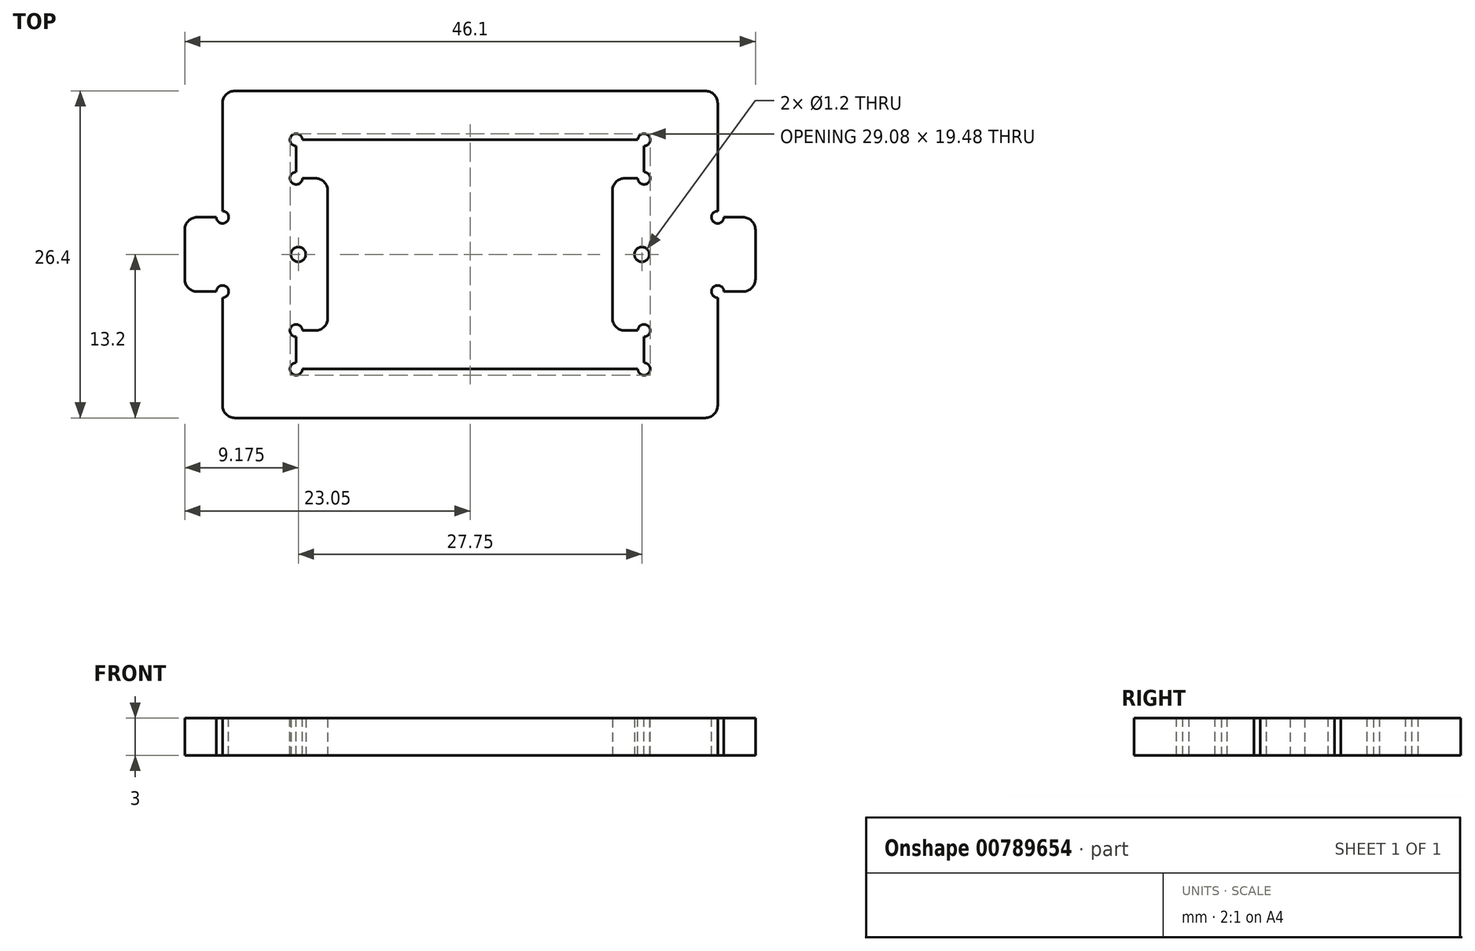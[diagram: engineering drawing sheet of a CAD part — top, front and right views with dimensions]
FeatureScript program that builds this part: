
annotation { "Feature Type Name" : "Feature", "Feature Type Description" : "" }
export const myFeature = defineFeature(function(context is Context, id is Id, definition is map)
    precondition{}
    {
        {
            var Q0;
            Q0=qCreatedBy(makeId("Top.planeOp"),FACE);
            var sketch = newSketch(context, id + "F0", { "sketchPlane" : qUnion([Q0])});
            skLineSegment(sketch, "E0", {"start": v(0, 0) * mm, "end": v(0, 13.2) * mm, "construction": true});
            skLineSegment(sketch, "E1.MirrorCS", {"start": v(-20, -13.2) * mm, "end": v(0, -13.2) * mm});
            skLineSegment(sketch, "E2.MirrorCS", {"start": v(20, -13.2) * mm, "end": v(0, -13.2) * mm});
            skCircle(sketch, "E3", {"center": v(-13.88, 0) * mm, "radius": 0.6 * mm});
            skCircle(sketch, "E4.MirrorC", {"center": v(13.88, 0) * mm, "radius": 0.6 * mm});
            skLineSegment(sketch, "E5", {"start": v(-20, 13.2) * mm, "end": v(20, 13.2) * mm});
            skLineSegment(sketch, "E6", {"start": v(-20, 13.2) * mm, "end": v(-20, -13.2) * mm});
            skLineSegment(sketch, "E7", {"start": v(20, 13.2) * mm, "end": v(20, -13.2) * mm});
            skLineSegment(sketch, "E8", {"start": v(0, 0) * mm, "end": v(-20, 0) * mm, "construction": true});
            skLineSegment(sketch, "E9.bottom", {"start": v(-14.05, 9.25) * mm, "end": v(14.05, 9.25) * mm});
            skLineSegment(sketch, "E9.top", {"start": v(-14.05, 6.15) * mm, "end": v(-11.5, 6.15) * mm});
            skLineSegment(sketch, "E9.left", {"start": v(-14.05, 9.25) * mm, "end": v(-14.05, 6.15) * mm});
            skLineSegment(sketch, "E9.right", {"start": v(14.05, 9.25) * mm, "end": v(14.05, 6.15) * mm});
            skLineSegment(sketch, "E10.MirrorCS", {"start": v(-14.05, -9.25) * mm, "end": v(14.05, -9.25) * mm});
            skLineSegment(sketch, "E11.MirrorCS", {"start": v(-14.05, -6.15) * mm, "end": v(-11.5, -6.15) * mm});
            skLineSegment(sketch, "E12.MirrorCS", {"start": v(-14.05, -9.25) * mm, "end": v(-14.05, -6.15) * mm});
            skLineSegment(sketch, "E13.MirrorCS", {"start": v(14.05, -9.25) * mm, "end": v(14.05, -6.15) * mm});
            skLineSegment(sketch, "E14", {"start": v(-11.5, 6.15) * mm, "end": v(-11.5, -6.15) * mm});
            skLineSegment(sketch, "E15", {"start": v(11.5, 6.15) * mm, "end": v(11.5, -6.15) * mm});
            skLineSegment(sketch, "E16.trimOffspring", {"start": v(11.5, 6.15) * mm, "end": v(14.05, 6.15) * mm});
            skLineSegment(sketch, "E17.trimOffspring", {"start": v(11.5, -6.15) * mm, "end": v(14.05, -6.15) * mm});
            skSolve(sketch);
        }
        {
            var Q0;
            Q0=makeQuery(id+"F0.imprint","IMPRINT",FACE,{"disambiguationData":[TD([[makeQuery(id+"F0.imprint","IMPRINT",EDGE,{"derivedFrom":sQuery(id+"F0.wireOp",EDGE,"E1.MirrorCS")}),1.0]])]});
            extrude(context, id + "F1", {"entities" : qUnion([Q0]), "depth" : 3 * mm, "offsetDistance" : 25 * mm});
        }
        {
            var Q0;
            Q0=makeQuery(id+"F1.opExtrude","CAP_FACE",FACE,{"disambiguationData":[OSD([sQuery(id+"F0.wireOp",EDGE,"E1.MirrorCS"),sQuery(id+"F0.wireOp",EDGE,"E2.MirrorCS"),sQuery(id+"F0.wireOp",EDGE,"E3"),sQuery(id+"F0.wireOp",EDGE,"E4.MirrorC"),sQuery(id+"F0.wireOp",EDGE,"E5"),sQuery(id+"F0.wireOp",EDGE,"E6"),sQuery(id+"F0.wireOp",EDGE,"E7"),sQuery(id+"F0.wireOp",EDGE,"E9.bottom"),sQuery(id+"F0.wireOp",EDGE,"E9.top"),sQuery(id+"F0.wireOp",EDGE,"E9.left"),sQuery(id+"F0.wireOp",EDGE,"E9.right"),sQuery(id+"F0.wireOp",EDGE,"E10.MirrorCS"),sQuery(id+"F0.wireOp",EDGE,"E11.MirrorCS"),sQuery(id+"F0.wireOp",EDGE,"E12.MirrorCS"),sQuery(id+"F0.wireOp",EDGE,"E13.MirrorCS"),sQuery(id+"F0.wireOp",EDGE,"E14"),sQuery(id+"F0.wireOp",EDGE,"E15"),sQuery(id+"F0.wireOp",EDGE,"E16.trimOffspring"),sQuery(id+"F0.wireOp",EDGE,"E17.trimOffspring")])],"isStart":true});
            var sketch = newSketch(context, id + "F2", { "sketchPlane" : qUnion([Q0])});
            skLineSegment(sketch, "E18.bottom", {"start": v(-20, -3) * mm, "end": v(-23.05, -3) * mm});
            skLineSegment(sketch, "E18.top", {"start": v(-20, 3) * mm, "end": v(-23.05, 3) * mm});
            skLineSegment(sketch, "E18.left", {"start": v(-20, -3) * mm, "end": v(-20, 3) * mm});
            skLineSegment(sketch, "E18.right", {"start": v(-23.05, -3) * mm, "end": v(-23.05, 3) * mm});
            skLineSegment(sketch, "E19.MirrorCS", {"start": v(20, 3) * mm, "end": v(23.05, 3) * mm});
            skLineSegment(sketch, "E20.MirrorCS", {"start": v(20, -3) * mm, "end": v(20, 3) * mm});
            skLineSegment(sketch, "E21.MirrorCS", {"start": v(23.05, -3) * mm, "end": v(23.05, 3) * mm});
            skLineSegment(sketch, "E22.MirrorCS", {"start": v(20, -3) * mm, "end": v(23.05, -3) * mm});
            skSolve(sketch);
        }
        {
            var Q0;
            Q0 = qSketchRegion(id + "F2", true);
            var Q1;
            Q1=makeQuery(id+"F1.opExtrude","CAP_FACE",FACE,{"disambiguationData":[OSD([sQuery(id+"F0.wireOp",EDGE,"E1.MirrorCS"),sQuery(id+"F0.wireOp",EDGE,"E2.MirrorCS"),sQuery(id+"F0.wireOp",EDGE,"E3"),sQuery(id+"F0.wireOp",EDGE,"E4.MirrorC"),sQuery(id+"F0.wireOp",EDGE,"E5"),sQuery(id+"F0.wireOp",EDGE,"E6"),sQuery(id+"F0.wireOp",EDGE,"E7"),sQuery(id+"F0.wireOp",EDGE,"E9.bottom"),sQuery(id+"F0.wireOp",EDGE,"E9.top"),sQuery(id+"F0.wireOp",EDGE,"E9.left"),sQuery(id+"F0.wireOp",EDGE,"E9.right"),sQuery(id+"F0.wireOp",EDGE,"E10.MirrorCS"),sQuery(id+"F0.wireOp",EDGE,"E11.MirrorCS"),sQuery(id+"F0.wireOp",EDGE,"E12.MirrorCS"),sQuery(id+"F0.wireOp",EDGE,"E13.MirrorCS"),sQuery(id+"F0.wireOp",EDGE,"E14"),sQuery(id+"F0.wireOp",EDGE,"E15"),sQuery(id+"F0.wireOp",EDGE,"E16.trimOffspring"),sQuery(id+"F0.wireOp",EDGE,"E17.trimOffspring")])],"isStart":false});
            extrude(context, id + "F3", {"entities" : qUnion([Q0]), "operationType" : NewBodyOperationType.ADD, "endBound" : BoundingType.UP_TO_SURFACE, "oppositeDirection" : true, "depth" : 25 * mm, "endBoundEntityFace" : qUnion([Q1]), "offsetDistance" : 25 * mm});
        }
        {
            var Q0;
            {var subQ0=sQuery(id+"F0.wireOp",EDGE,"E17.trimOffspring");var subQ1=sQuery(id+"F0.wireOp",EDGE,"E16.trimOffspring");var subQ2=sQuery(id+"F0.wireOp",EDGE,"E15");var subQ3=sQuery(id+"F0.wireOp",EDGE,"E14");var subQ4=sQuery(id+"F0.wireOp",EDGE,"E13.MirrorCS");var subQ5=sQuery(id+"F0.wireOp",EDGE,"E12.MirrorCS");var subQ6=sQuery(id+"F0.wireOp",EDGE,"E11.MirrorCS");var subQ7=sQuery(id+"F0.wireOp",EDGE,"E10.MirrorCS");var subQ8=sQuery(id+"F0.wireOp",EDGE,"E9.right");var subQ9=sQuery(id+"F0.wireOp",EDGE,"E9.left");var subQ10=sQuery(id+"F0.wireOp",EDGE,"E9.top");var subQ11=sQuery(id+"F0.wireOp",EDGE,"E9.bottom");var subQ12=sQuery(id+"F0.wireOp",EDGE,"E7");var subQ13=sQuery(id+"F0.wireOp",EDGE,"E6");var subQ14=sQuery(id+"F0.wireOp",EDGE,"E5");var subQ15=sQuery(id+"F0.wireOp",EDGE,"E4.MirrorC");var subQ16=sQuery(id+"F0.wireOp",EDGE,"E3");var subQ17=sQuery(id+"F0.wireOp",EDGE,"E2.MirrorCS");var subQ18=sQuery(id+"F0.wireOp",EDGE,"E1.MirrorCS");Q0=makeQuery(id+"F3.boolean.opBoolean","MERGE",FACE,{"derivedFrom":[makeQuery(id+"F1.opExtrude","CAP_FACE",FACE,{"disambiguationData":[OSD([subQ18,subQ17,subQ16,subQ15,subQ14,subQ13,subQ12,subQ11,subQ10,subQ9,subQ8,subQ7,subQ6,subQ5,subQ4,subQ3,subQ2,subQ1,subQ0])],"isStart":false}),makeQuery(id+"F3.opExtrude","CAP_FACE",FACE,{"disambiguationData":[OSD([subQ18,subQ17,subQ16,subQ15,subQ14,subQ13,subQ12,subQ11,subQ10,subQ9,subQ8,subQ7,subQ6,subQ5,subQ4,subQ3,subQ2,subQ1,subQ0]),OD(0.0)],"isStart":false}),makeQuery(id+"F3.opExtrude","CAP_FACE",FACE,{"disambiguationData":[OSD([subQ18,subQ17,subQ16,subQ15,subQ14,subQ13,subQ12,subQ11,subQ10,subQ9,subQ8,subQ7,subQ6,subQ5,subQ4,subQ3,subQ2,subQ1,subQ0]),OD(1.0)],"isStart":false})]});}
            var sketch = newSketch(context, id + "F4", { "sketchPlane" : qUnion([Q0])});
            skPoint(sketch, "E23", {"position": v(-20, 3) * mm});
            skPoint(sketch, "E24", {"position": v(-20, -3) * mm});
            skPoint(sketch, "E25", {"position": v(-14.05, -6.15) * mm});
            skPoint(sketch, "E26", {"position": v(-14.05, -9.25) * mm});
            skPoint(sketch, "E27", {"position": v(-14.05, 9.25) * mm});
            skPoint(sketch, "E28", {"position": v(-14.05, 6.15) * mm});
            skPoint(sketch, "E29", {"position": v(14.05, 9.25) * mm});
            skPoint(sketch, "E30", {"position": v(14.05, 6.15) * mm});
            skPoint(sketch, "E31", {"position": v(14.05, -6.15) * mm});
            skPoint(sketch, "E32", {"position": v(14.05, -9.25) * mm});
            skPoint(sketch, "E33", {"position": v(20, -3) * mm});
            skPoint(sketch, "E34", {"position": v(20, 3) * mm});
            skSolve(sketch);
        }
        {
            var Q0;
            Q0=sQuery(id+"F4.wireOp",VERTEX,"E27");
            var Q1;
            Q1=sQuery(id+"F4.wireOp",VERTEX,"E28");
            var Q2;
            Q2=sQuery(id+"F4.wireOp",VERTEX,"E23");
            var Q3;
            Q3=sQuery(id+"F4.wireOp",VERTEX,"E24");
            var Q4;
            Q4=sQuery(id+"F4.wireOp",VERTEX,"E25");
            var Q5;
            Q5=sQuery(id+"F4.wireOp",VERTEX,"E26");
            var Q6;
            Q6=sQuery(id+"F4.wireOp",VERTEX,"E31");
            var Q7;
            Q7=sQuery(id+"F4.wireOp",VERTEX,"E32");
            var Q8;
            Q8=sQuery(id+"F4.wireOp",VERTEX,"E33");
            var Q9;
            Q9=sQuery(id+"F4.wireOp",VERTEX,"E34");
            var Q10;
            Q10=sQuery(id+"F4.wireOp",VERTEX,"E30");
            var Q11;
            Q11=sQuery(id+"F4.wireOp",VERTEX,"E29");
            var Q12;
            Q12=makeQuery(id+"F1.opExtrude","SWEPT_BODY",BODY,{"disambiguationData":[OSD([sQuery(id+"F0.wireOp",EDGE,"E1.MirrorCS"),sQuery(id+"F0.wireOp",EDGE,"E2.MirrorCS"),sQuery(id+"F0.wireOp",EDGE,"E3"),sQuery(id+"F0.wireOp",EDGE,"E4.MirrorC"),sQuery(id+"F0.wireOp",EDGE,"E5"),sQuery(id+"F0.wireOp",EDGE,"E6"),sQuery(id+"F0.wireOp",EDGE,"E7"),sQuery(id+"F0.wireOp",EDGE,"E9.bottom"),sQuery(id+"F0.wireOp",EDGE,"E9.top"),sQuery(id+"F0.wireOp",EDGE,"E9.left"),sQuery(id+"F0.wireOp",EDGE,"E9.right"),sQuery(id+"F0.wireOp",EDGE,"E10.MirrorCS"),sQuery(id+"F0.wireOp",EDGE,"E11.MirrorCS"),sQuery(id+"F0.wireOp",EDGE,"E12.MirrorCS"),sQuery(id+"F0.wireOp",EDGE,"E13.MirrorCS"),sQuery(id+"F0.wireOp",EDGE,"E14"),sQuery(id+"F0.wireOp",EDGE,"E15"),sQuery(id+"F0.wireOp",EDGE,"E16.trimOffspring"),sQuery(id+"F0.wireOp",EDGE,"E17.trimOffspring")])]});
            hole(context, id + "F5", {"style" : HoleStyle.SIMPLE, "endStyle" : HoleEndStyle.THROUGH, "holeDiameter" : 1 * mm, "majorDiameter" : 5 * mm, "isTappedThrough" : true, "tappedDepth" : 12 * mm, "tapClearance" : 3, "locations" : qUnion([Q0, Q1, Q2, Q3, Q4, Q5, Q6, Q7, Q8, Q9, Q10, Q11]), "scope" : qUnion([Q12])});
        }
        {
            var Q0;
            Q0=makeQuery(id+"F1.opExtrude","SWEPT_EDGE",EDGE,{"disambiguationData":[OSD([sQuery(id+"F0.wireOp",EDGE,"E5"),sQuery(id+"F0.wireOp",EDGE,"E6")])]});
            var Q1;
            {var subQ14=sQuery(id+"F0.wireOp",EDGE,"E6");var subQ15=sQuery(id+"F0.wireOp",EDGE,"E5");Q1=makeQuery(id+"F5.hole-2.boolean.opBoolean","INTERSECT",EDGE,{"derivedFrom":[makeQuery(id+"F3.boolean.opBoolean","SPLIT",FACE,{"disambiguationData":[TD([makeQuery(id+"F1.opExtrude","SWEPT_FACE",FACE,{"disambiguationData":[OSD([subQ15])]})])],"derivedFrom":makeQuery(id+"F1.opExtrude","SWEPT_FACE",FACE,{"disambiguationData":[OSD([subQ14])]})}),makeQuery(id+"F5.hole-2.opRevolve","SWEPT_FACE",FACE,{"disambiguationData":[OSD([sQuery(id+"F5.hole-2.sketch.wireOp",EDGE,"core_line_2")])]})]});}
            var Q2;
            Q2=makeQuery(id+"F5.hole-2.boolean.opBoolean","INTERSECT",EDGE,{"derivedFrom":[makeQuery(id+"F3.opExtrude","SWEPT_FACE",FACE,{"disambiguationData":[OSD([sQuery(id+"F2.wireOp",EDGE,"E18.bottom")])]}),makeQuery(id+"F5.hole-2.opRevolve","SWEPT_FACE",FACE,{"disambiguationData":[OSD([sQuery(id+"F5.hole-2.sketch.wireOp",EDGE,"core_line_2")])]})]});
            var Q3;
            Q3=makeQuery(id+"F3.opExtrude","SWEPT_EDGE",EDGE,{"disambiguationData":[OSD([sQuery(id+"F2.wireOp",EDGE,"E18.bottom"),sQuery(id+"F2.wireOp",EDGE,"E18.right")])]});
            var Q4;
            Q4=makeQuery(id+"F3.opExtrude","SWEPT_EDGE",EDGE,{"disambiguationData":[OSD([sQuery(id+"F2.wireOp",EDGE,"E18.top"),sQuery(id+"F2.wireOp",EDGE,"E18.right")])]});
            var Q5;
            {var subQ0=sQuery(id+"F2.wireOp",EDGE,"E18.top");var subQ14=sQuery(id+"F0.wireOp",EDGE,"E6");Q5=makeQuery(id+"F5.hole-3.boolean.opBoolean","INTERSECT",EDGE,{"derivedFrom":[makeQuery(id+"F3.boolean.opBoolean","SPLIT",FACE,{"disambiguationData":[TD([makeQuery(id+"F3.opExtrude","SWEPT_FACE",FACE,{"disambiguationData":[OSD([subQ0])]})])],"derivedFrom":makeQuery(id+"F1.opExtrude","SWEPT_FACE",FACE,{"disambiguationData":[OSD([subQ14])]})}),makeQuery(id+"F5.hole-3.opRevolve","SWEPT_FACE",FACE,{"disambiguationData":[OSD([sQuery(id+"F5.hole-3.sketch.wireOp",EDGE,"core_line_2")])]})]});}
            var Q6;
            Q6=makeQuery(id+"F1.opExtrude","SWEPT_EDGE",EDGE,{"disambiguationData":[OSD([sQuery(id+"F0.wireOp",EDGE,"E1.MirrorCS"),sQuery(id+"F0.wireOp",EDGE,"E6")])]});
            var Q7;
            Q7=makeQuery(id+"F5.hole-5.boolean.opBoolean","INTERSECT",EDGE,{"derivedFrom":[makeQuery(id+"F1.opExtrude","SWEPT_FACE",FACE,{"disambiguationData":[OSD([sQuery(id+"F0.wireOp",EDGE,"E10.MirrorCS")])]}),makeQuery(id+"F5.hole-5.opRevolve","SWEPT_FACE",FACE,{"disambiguationData":[OSD([sQuery(id+"F5.hole-5.sketch.wireOp",EDGE,"core_line_2")])]})]});
            var Q8;
            Q8=makeQuery(id+"F5.hole-4.boolean.opBoolean","INTERSECT",EDGE,{"derivedFrom":[makeQuery(id+"F1.opExtrude","SWEPT_FACE",FACE,{"disambiguationData":[OSD([sQuery(id+"F0.wireOp",EDGE,"E12.MirrorCS")])]}),makeQuery(id+"F5.hole-4.opRevolve","SWEPT_FACE",FACE,{"disambiguationData":[OSD([sQuery(id+"F5.hole-4.sketch.wireOp",EDGE,"core_line_2")])]})]});
            var Q9;
            Q9=makeQuery(id+"F5.hole-1.boolean.opBoolean","INTERSECT",EDGE,{"derivedFrom":[makeQuery(id+"F1.opExtrude","SWEPT_FACE",FACE,{"disambiguationData":[OSD([sQuery(id+"F0.wireOp",EDGE,"E9.top")])]}),makeQuery(id+"F5.hole-1.opRevolve","SWEPT_FACE",FACE,{"disambiguationData":[OSD([sQuery(id+"F5.hole-1.sketch.wireOp",EDGE,"core_line_2")])]})]});
            var Q10;
            Q10=makeQuery(id+"F1.opExtrude","SWEPT_EDGE",EDGE,{"disambiguationData":[OSD([sQuery(id+"F0.wireOp",EDGE,"E9.top"),sQuery(id+"F0.wireOp",EDGE,"E14")])]});
            var Q11;
            Q11=makeQuery(id+"F5.hole-0.boolean.opBoolean","INTERSECT",EDGE,{"derivedFrom":[makeQuery(id+"F1.opExtrude","SWEPT_FACE",FACE,{"disambiguationData":[OSD([sQuery(id+"F0.wireOp",EDGE,"E9.left")])]}),makeQuery(id+"F5.hole-0.opRevolve","SWEPT_FACE",FACE,{"disambiguationData":[OSD([sQuery(id+"F5.hole-0.sketch.wireOp",EDGE,"core_line_2")])]})]});
            var Q12;
            Q12=makeQuery(id+"F5.hole-7.boolean.opBoolean","INTERSECT",EDGE,{"derivedFrom":[makeQuery(id+"F1.opExtrude","SWEPT_FACE",FACE,{"disambiguationData":[OSD([sQuery(id+"F0.wireOp",EDGE,"E10.MirrorCS")])]}),makeQuery(id+"F5.hole-7.opRevolve","SWEPT_FACE",FACE,{"disambiguationData":[OSD([sQuery(id+"F5.hole-7.sketch.wireOp",EDGE,"core_line_2")])]})]});
            var Q13;
            Q13=makeQuery(id+"F5.hole-6.boolean.opBoolean","INTERSECT",EDGE,{"derivedFrom":[makeQuery(id+"F1.opExtrude","SWEPT_FACE",FACE,{"disambiguationData":[OSD([sQuery(id+"F0.wireOp",EDGE,"E13.MirrorCS")])]}),makeQuery(id+"F5.hole-6.opRevolve","SWEPT_FACE",FACE,{"disambiguationData":[OSD([sQuery(id+"F5.hole-6.sketch.wireOp",EDGE,"core_line_2")])]})]});
            var Q14;
            Q14=makeQuery(id+"F1.opExtrude","SWEPT_EDGE",EDGE,{"disambiguationData":[OSD([sQuery(id+"F0.wireOp",EDGE,"E15"),sQuery(id+"F0.wireOp",EDGE,"E17.trimOffspring")])]});
            var Q15;
            Q15=makeQuery(id+"F1.opExtrude","SWEPT_EDGE",EDGE,{"disambiguationData":[OSD([sQuery(id+"F0.wireOp",EDGE,"E15"),sQuery(id+"F0.wireOp",EDGE,"E16.trimOffspring")])]});
            var Q16;
            Q16=makeQuery(id+"F5.hole-10.boolean.opBoolean","INTERSECT",EDGE,{"derivedFrom":[makeQuery(id+"F1.opExtrude","SWEPT_FACE",FACE,{"disambiguationData":[OSD([sQuery(id+"F0.wireOp",EDGE,"E16.trimOffspring")])]}),makeQuery(id+"F5.hole-10.opRevolve","SWEPT_FACE",FACE,{"disambiguationData":[OSD([sQuery(id+"F5.hole-10.sketch.wireOp",EDGE,"core_line_2")])]})]});
            var Q17;
            Q17=makeQuery(id+"F5.hole-11.boolean.opBoolean","INTERSECT",EDGE,{"derivedFrom":[makeQuery(id+"F1.opExtrude","SWEPT_FACE",FACE,{"disambiguationData":[OSD([sQuery(id+"F0.wireOp",EDGE,"E9.right")])]}),makeQuery(id+"F5.hole-11.opRevolve","SWEPT_FACE",FACE,{"disambiguationData":[OSD([sQuery(id+"F5.hole-11.sketch.wireOp",EDGE,"core_line_2")])]})]});
            var Q18;
            Q18=makeQuery(id+"F3.opExtrude","SWEPT_EDGE",EDGE,{"disambiguationData":[OSD([sQuery(id+"F2.wireOp",EDGE,"E21.MirrorCS"),sQuery(id+"F2.wireOp",EDGE,"E22.MirrorCS")])]});
            var Q19;
            Q19=makeQuery(id+"F1.opExtrude","SWEPT_EDGE",EDGE,{"disambiguationData":[OSD([sQuery(id+"F0.wireOp",EDGE,"E5"),sQuery(id+"F0.wireOp",EDGE,"E7")])]});
            var Q20;
            Q20=makeQuery(id+"F5.hole-9.boolean.opBoolean","INTERSECT",EDGE,{"derivedFrom":[makeQuery(id+"F3.opExtrude","SWEPT_FACE",FACE,{"disambiguationData":[OSD([sQuery(id+"F2.wireOp",EDGE,"E22.MirrorCS")])]}),makeQuery(id+"F5.hole-9.opRevolve","SWEPT_FACE",FACE,{"disambiguationData":[OSD([sQuery(id+"F5.hole-9.sketch.wireOp",EDGE,"core_line_2")])]})]});
            var Q21;
            {var subQ12=sQuery(id+"F0.wireOp",EDGE,"E7");var subQ14=sQuery(id+"F0.wireOp",EDGE,"E5");Q21=makeQuery(id+"F5.hole-9.boolean.opBoolean","INTERSECT",EDGE,{"derivedFrom":[makeQuery(id+"F3.boolean.opBoolean","SPLIT",FACE,{"disambiguationData":[TD([makeQuery(id+"F1.opExtrude","SWEPT_FACE",FACE,{"disambiguationData":[OSD([subQ14])]})])],"derivedFrom":makeQuery(id+"F1.opExtrude","SWEPT_FACE",FACE,{"disambiguationData":[OSD([subQ12])]})}),makeQuery(id+"F5.hole-9.opRevolve","SWEPT_FACE",FACE,{"disambiguationData":[OSD([sQuery(id+"F5.hole-9.sketch.wireOp",EDGE,"core_line_2")])]})]});}
            var Q22;
            Q22=makeQuery(id+"F5.hole-8.boolean.opBoolean","INTERSECT",EDGE,{"derivedFrom":[makeQuery(id+"F3.opExtrude","SWEPT_FACE",FACE,{"disambiguationData":[OSD([sQuery(id+"F2.wireOp",EDGE,"E19.MirrorCS")])]}),makeQuery(id+"F5.hole-8.opRevolve","SWEPT_FACE",FACE,{"disambiguationData":[OSD([sQuery(id+"F5.hole-8.sketch.wireOp",EDGE,"core_line_2")])]})]});
            var Q23;
            Q23=makeQuery(id+"F3.opExtrude","SWEPT_EDGE",EDGE,{"disambiguationData":[OSD([sQuery(id+"F2.wireOp",EDGE,"E19.MirrorCS"),sQuery(id+"F2.wireOp",EDGE,"E21.MirrorCS")])]});
            var Q24;
            {var subQ12=sQuery(id+"F0.wireOp",EDGE,"E7");var subQ19=sQuery(id+"F2.wireOp",EDGE,"E19.MirrorCS");Q24=makeQuery(id+"F5.hole-8.boolean.opBoolean","INTERSECT",EDGE,{"derivedFrom":[makeQuery(id+"F3.boolean.opBoolean","SPLIT",FACE,{"disambiguationData":[TD([makeQuery(id+"F3.opExtrude","SWEPT_FACE",FACE,{"disambiguationData":[OSD([subQ19])]})])],"derivedFrom":makeQuery(id+"F1.opExtrude","SWEPT_FACE",FACE,{"disambiguationData":[OSD([subQ12])]})}),makeQuery(id+"F5.hole-8.opRevolve","SWEPT_FACE",FACE,{"disambiguationData":[OSD([sQuery(id+"F5.hole-8.sketch.wireOp",EDGE,"core_line_2")])]})]});}
            var Q25;
            Q25=makeQuery(id+"F5.hole-6.boolean.opBoolean","INTERSECT",EDGE,{"derivedFrom":[makeQuery(id+"F1.opExtrude","SWEPT_FACE",FACE,{"disambiguationData":[OSD([sQuery(id+"F0.wireOp",EDGE,"E17.trimOffspring")])]}),makeQuery(id+"F5.hole-6.opRevolve","SWEPT_FACE",FACE,{"disambiguationData":[OSD([sQuery(id+"F5.hole-6.sketch.wireOp",EDGE,"core_line_2")])]})]});
            var Q26;
            Q26=makeQuery(id+"F1.opExtrude","SWEPT_EDGE",EDGE,{"disambiguationData":[OSD([sQuery(id+"F0.wireOp",EDGE,"E2.MirrorCS"),sQuery(id+"F0.wireOp",EDGE,"E7")])]});
            var Q27;
            Q27=makeQuery(id+"F5.hole-11.boolean.opBoolean","INTERSECT",EDGE,{"derivedFrom":[makeQuery(id+"F1.opExtrude","SWEPT_FACE",FACE,{"disambiguationData":[OSD([sQuery(id+"F0.wireOp",EDGE,"E9.bottom")])]}),makeQuery(id+"F5.hole-11.opRevolve","SWEPT_FACE",FACE,{"disambiguationData":[OSD([sQuery(id+"F5.hole-11.sketch.wireOp",EDGE,"core_line_2")])]})]});
            var Q28;
            Q28=makeQuery(id+"F5.hole-5.boolean.opBoolean","INTERSECT",EDGE,{"derivedFrom":[makeQuery(id+"F1.opExtrude","SWEPT_FACE",FACE,{"disambiguationData":[OSD([sQuery(id+"F0.wireOp",EDGE,"E12.MirrorCS")])]}),makeQuery(id+"F5.hole-5.opRevolve","SWEPT_FACE",FACE,{"disambiguationData":[OSD([sQuery(id+"F5.hole-5.sketch.wireOp",EDGE,"core_line_2")])]})]});
            var Q29;
            Q29=makeQuery(id+"F5.hole-4.boolean.opBoolean","INTERSECT",EDGE,{"derivedFrom":[makeQuery(id+"F1.opExtrude","SWEPT_FACE",FACE,{"disambiguationData":[OSD([sQuery(id+"F0.wireOp",EDGE,"E11.MirrorCS")])]}),makeQuery(id+"F5.hole-4.opRevolve","SWEPT_FACE",FACE,{"disambiguationData":[OSD([sQuery(id+"F5.hole-4.sketch.wireOp",EDGE,"core_line_2")])]})]});
            var Q30;
            Q30=makeQuery(id+"F1.opExtrude","SWEPT_EDGE",EDGE,{"disambiguationData":[OSD([sQuery(id+"F0.wireOp",EDGE,"E11.MirrorCS"),sQuery(id+"F0.wireOp",EDGE,"E14")])]});
            var Q31;
            Q31=makeQuery(id+"F5.hole-3.boolean.opBoolean","INTERSECT",EDGE,{"derivedFrom":[makeQuery(id+"F3.opExtrude","SWEPT_FACE",FACE,{"disambiguationData":[OSD([sQuery(id+"F2.wireOp",EDGE,"E18.top")])]}),makeQuery(id+"F5.hole-3.opRevolve","SWEPT_FACE",FACE,{"disambiguationData":[OSD([sQuery(id+"F5.hole-3.sketch.wireOp",EDGE,"core_line_2")])]})]});
            var Q32;
            Q32=makeQuery(id+"F5.hole-1.boolean.opBoolean","INTERSECT",EDGE,{"derivedFrom":[makeQuery(id+"F1.opExtrude","SWEPT_FACE",FACE,{"disambiguationData":[OSD([sQuery(id+"F0.wireOp",EDGE,"E9.left")])]}),makeQuery(id+"F5.hole-1.opRevolve","SWEPT_FACE",FACE,{"disambiguationData":[OSD([sQuery(id+"F5.hole-1.sketch.wireOp",EDGE,"core_line_2")])]})]});
            var Q33;
            Q33=makeQuery(id+"F5.hole-0.boolean.opBoolean","INTERSECT",EDGE,{"derivedFrom":[makeQuery(id+"F1.opExtrude","SWEPT_FACE",FACE,{"disambiguationData":[OSD([sQuery(id+"F0.wireOp",EDGE,"E9.bottom")])]}),makeQuery(id+"F5.hole-0.opRevolve","SWEPT_FACE",FACE,{"disambiguationData":[OSD([sQuery(id+"F5.hole-0.sketch.wireOp",EDGE,"core_line_2")])]})]});
            var Q34;
            Q34=makeQuery(id+"F5.hole-7.boolean.opBoolean","INTERSECT",EDGE,{"derivedFrom":[makeQuery(id+"F1.opExtrude","SWEPT_FACE",FACE,{"disambiguationData":[OSD([sQuery(id+"F0.wireOp",EDGE,"E13.MirrorCS")])]}),makeQuery(id+"F5.hole-7.opRevolve","SWEPT_FACE",FACE,{"disambiguationData":[OSD([sQuery(id+"F5.hole-7.sketch.wireOp",EDGE,"core_line_2")])]})]});
            var Q35;
            Q35=makeQuery(id+"F5.hole-10.boolean.opBoolean","INTERSECT",EDGE,{"derivedFrom":[makeQuery(id+"F1.opExtrude","SWEPT_FACE",FACE,{"disambiguationData":[OSD([sQuery(id+"F0.wireOp",EDGE,"E9.right")])]}),makeQuery(id+"F5.hole-10.opRevolve","SWEPT_FACE",FACE,{"disambiguationData":[OSD([sQuery(id+"F5.hole-10.sketch.wireOp",EDGE,"core_line_2")])]})]});
            fillet(context, id + "F6", {"entities" : qUnion([Q0, Q1, Q2, Q3, Q4, Q5, Q6, Q7, Q8, Q9, Q10, Q11, Q12, Q13, Q14, Q15, Q16, Q17, Q18, Q19, Q20, Q21, Q22, Q23, Q24, Q25, Q26, Q27, Q28, Q29, Q30, Q31, Q32, Q33, Q34, Q35]), "radius" : 1 * mm, "tangentPropagation" : true, "allowEdgeOverflow" : false});
        }
    });
